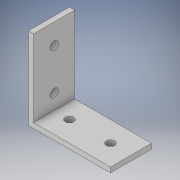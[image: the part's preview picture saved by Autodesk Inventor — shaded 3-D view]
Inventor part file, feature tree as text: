
AUTODESK INVENTOR PART (.ipt)
format: ipt  version: 2018 (Build 220112000, 112)  size: 120,320 bytes
history: native  units: in
note: dims shown in document units (in); Inventor stores cm internally (conversion verified against a paired STEP export)
features: extrude x3, sketch x3
ambient origin geometry x8: Origin, YZ Plane, XZ Plane, XY Plane, X Axis, Y Axis, Z Axis, Center Point
bodies: Solid1 (feature_tree)
feature tree (6):
  extrude  "Extrusion1"  Depth=2.0in
  extrude  "Extrusion2"  Depth=0.125in
  extrude  "Extrusion3"  Depth=1.0in
  sketch  "Sketch1"  dims[d0=0.125in d1=2.0in]
  sketch  "Sketch2"  dims[d2=2.0in d3=0.125in]
  sketch  "Sketch3"  dims[d4=1.0in d5=0.0in d6=0.5in d7=1.0in d8=0.2031in d9=1.0in d10=0.0in d11=0.5in d12=1.0in d13=0.2031in d14=1.0in d15=0.0in]
